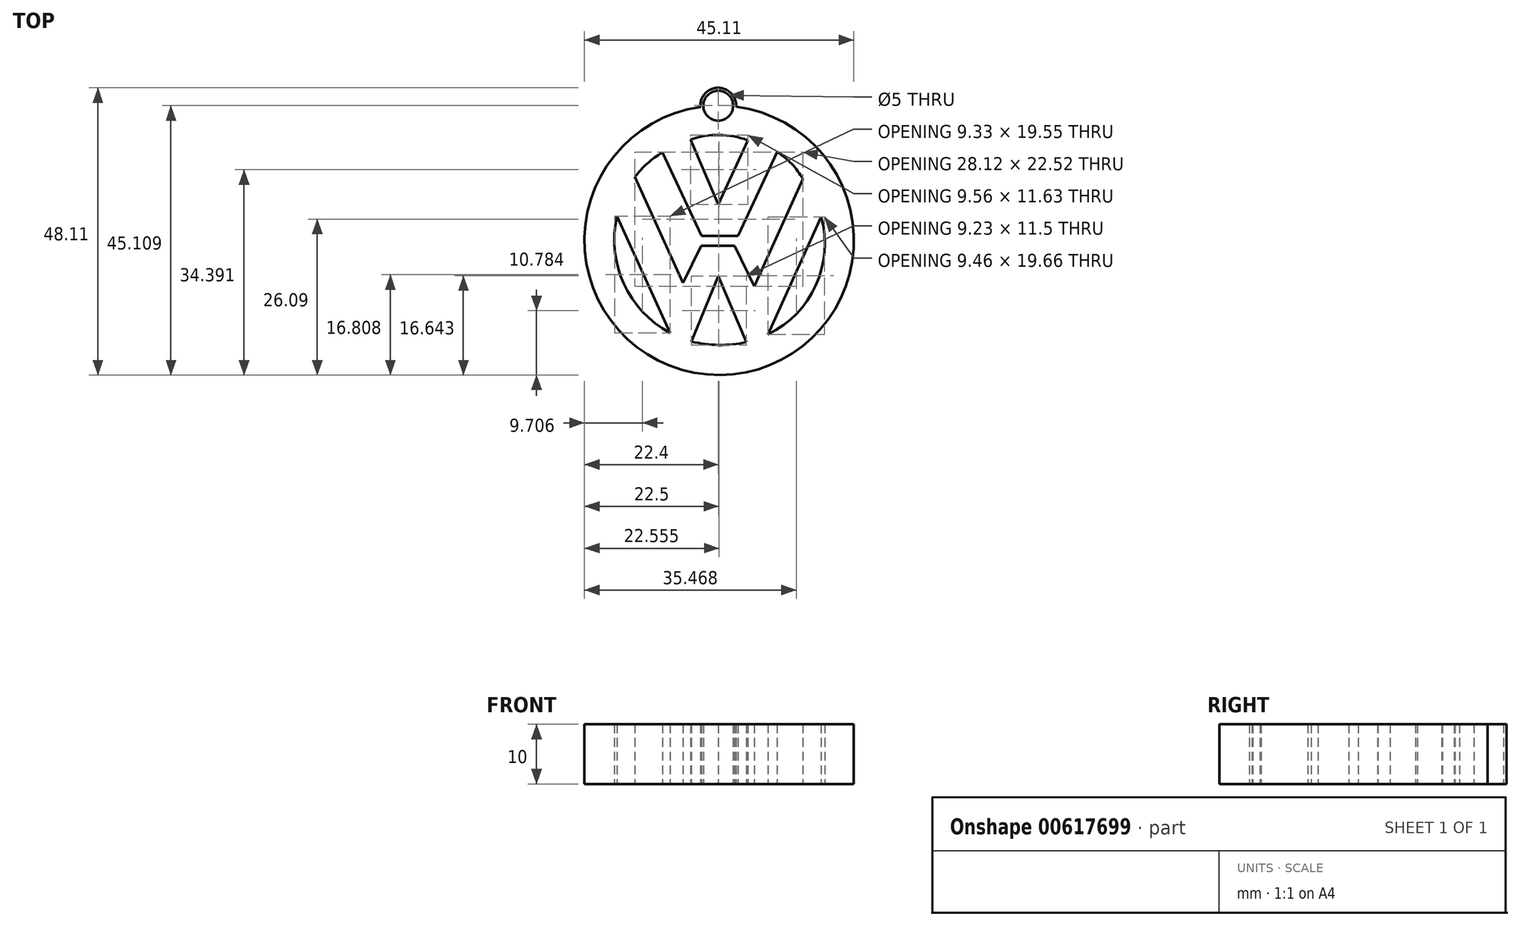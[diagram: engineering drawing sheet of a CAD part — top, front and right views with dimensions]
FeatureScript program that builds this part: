
annotation { "Feature Type Name" : "Feature", "Feature Type Description" : "" }
export const myFeature = defineFeature(function(context is Context, id is Id, definition is map)
    precondition{}
    {
        {
            var Q0;
            Q0=qCreatedBy(makeId("Top.planeOp"),FACE);
            var sketch = newSketch(context, id + "F0", { "sketchPlane" : qUnion([Q0])});
            skArc(sketch, "E0", {"start": v(4.93, 16.82) * mm, "mid": v(0.16, 17.7) * mm, "end": v(-4.62, 16.93) * mm});
            skArc(sketch, "E1", {"start": v(-4.51, -16.9) * mm, "mid": v(0.1, -17.48) * mm, "end": v(4.71, -17.02) * mm});
            skArc(sketch, "E2", {"start": v(8.34, -15.7) * mm, "mid": v(16.35, -7.48) * mm, "end": v(17.24, 3.96) * mm});
            skArc(sketch, "E3", {"start": v(-16.93, 4.07) * mm, "mid": v(-15.82, -7.22) * mm, "end": v(-8.03, -15.48) * mm});
            skArc(sketch, "E4", {"start": v(-9.35, 14.73) * mm, "mid": v(-11.87, 12.94) * mm, "end": v(-13.96, 10.67) * mm});
            skArc(sketch, "E5", {"start": v(14.16, 10.34) * mm, "mid": v(12.3, 12.85) * mm, "end": v(9.88, 14.84) * mm});
            skLineSegment(sketch, "E6", {"start": v(-16.93, 4.07) * mm, "end": v(-8.03, -15.48) * mm});
            skLineSegment(sketch, "E7", {"start": v(-13.96, 10.67) * mm, "end": v(-5.88, -7.1) * mm});
            skLineSegment(sketch, "E8", {"start": v(-5.88, -7.1) * mm, "end": v(-2.87, -0.87) * mm});
            skLineSegment(sketch, "E9", {"start": v(-2.87, -0.87) * mm, "end": v(2.74, -0.87) * mm});
            skLineSegment(sketch, "E10", {"start": v(2.74, -0.87) * mm, "end": v(6.03, -7.68) * mm});
            skLineSegment(sketch, "E11", {"start": v(6.03, -7.68) * mm, "end": v(14.16, 10.34) * mm});
            skLineSegment(sketch, "E12", {"start": v(9.88, 14.84) * mm, "end": v(3.33, 0.78) * mm});
            skLineSegment(sketch, "E13", {"start": v(3.33, 0.78) * mm, "end": v(-2.81, 0.78) * mm});
            skLineSegment(sketch, "E14", {"start": v(-2.81, 0.78) * mm, "end": v(-9.35, 14.73) * mm});
            skLineSegment(sketch, "E15", {"start": v(-4.62, 16.93) * mm, "end": v(0, 6.07) * mm});
            skLineSegment(sketch, "E16", {"start": v(0, 6.07) * mm, "end": v(4.93, 16.82) * mm});
            skLineSegment(sketch, "E17", {"start": v(-4.51, -16.9) * mm, "end": v(0, -5.97) * mm});
            skLineSegment(sketch, "E18", {"start": v(0, -5.97) * mm, "end": v(4.71, -17.02) * mm});
            skLineSegment(sketch, "E19", {"start": v(17.24, 3.96) * mm, "end": v(8.34, -15.7) * mm});
            skArc(sketch, "E20", {"start": v(-2.5, 22.44) * mm, "mid": v(0.3, -22.5) * mm, "end": v(2.5, 22.48) * mm});
            skArc(sketch, "E21", {"start": v(3, 22.42) * mm, "mid": v(-0.02, 25.6) * mm, "end": v(-3, 22.38) * mm});
            skCircle(sketch, "E22", {"center": v(0, 22.6) * mm, "radius": 2.5 * mm});
            skSolve(sketch);
        }
        {
            var Q0;
            Q0 = qSketchRegion(id + "F0", true);
            extrude(context, id + "F1", {"entities" : qUnion([Q0]), "depth" : 10 * mm, "offsetDistance" : 25 * mm});
        }
    });
